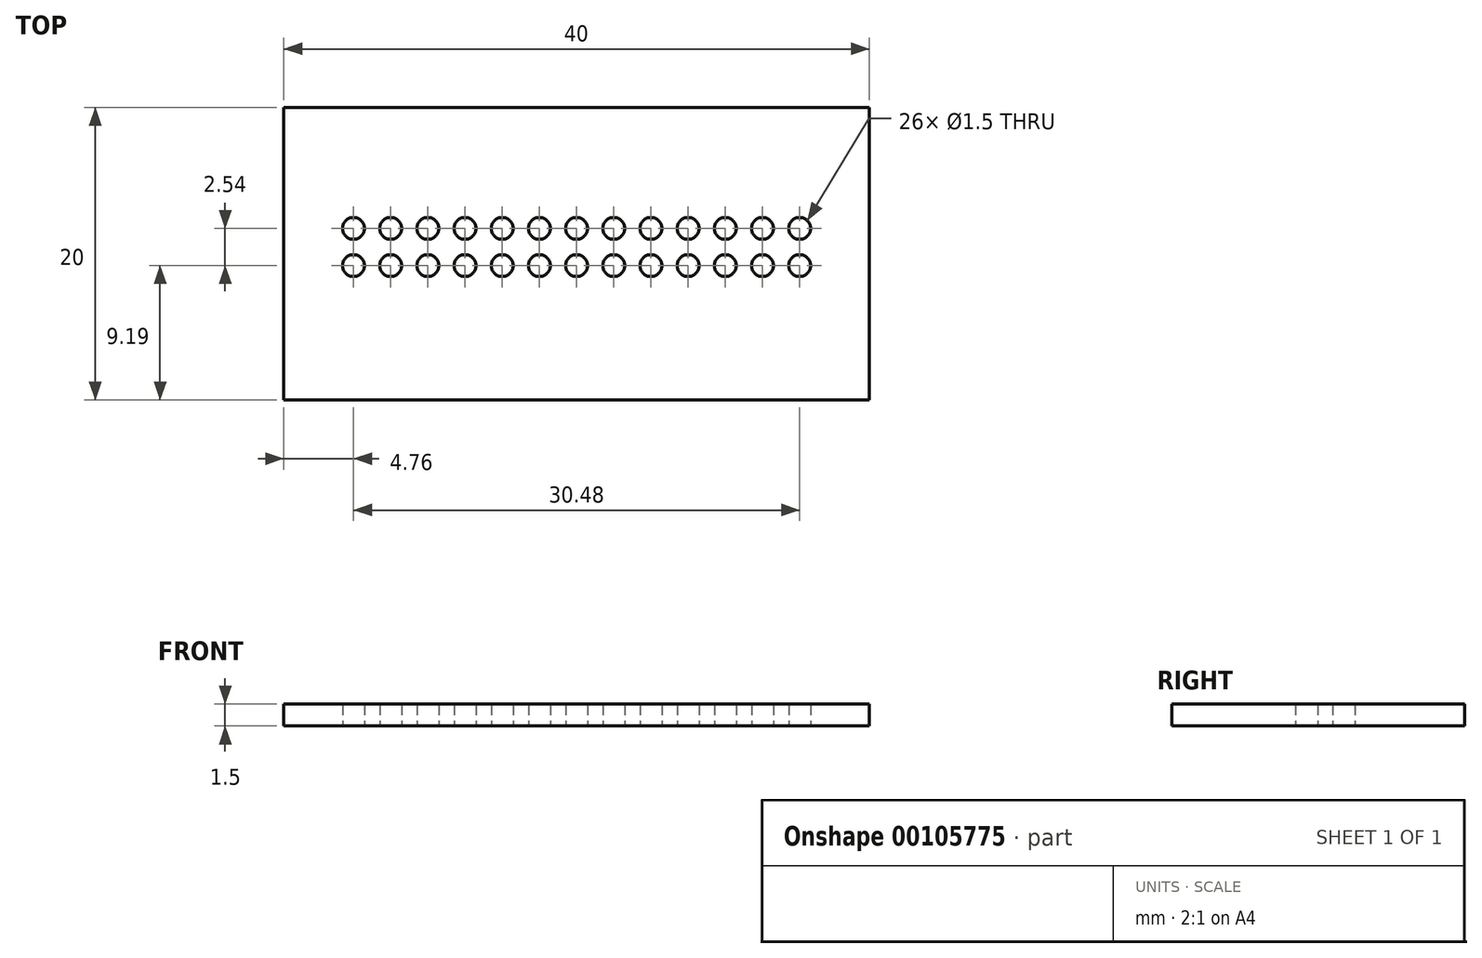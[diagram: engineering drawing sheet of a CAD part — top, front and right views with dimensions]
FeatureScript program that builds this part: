
annotation { "Feature Type Name" : "Feature", "Feature Type Description" : "" }
export const myFeature = defineFeature(function(context is Context, id is Id, definition is map)
    precondition{}
    {
        {
            var Q0;
            Q0=qCreatedBy(makeId("Top.planeOp"),FACE);
            var sketch = newSketch(context, id + "F0", { "sketchPlane" : qUnion([Q0])});
            skLineSegment(sketch, "E0.bottom", {"start": v(-20, 10) * mm, "end": v(20, 10) * mm});
            skLineSegment(sketch, "E0.top", {"start": v(-20, -10) * mm, "end": v(20, -10) * mm});
            skLineSegment(sketch, "E0.left", {"start": v(-20, 10) * mm, "end": v(-20, -10) * mm});
            skLineSegment(sketch, "E0.right", {"start": v(20, 10) * mm, "end": v(20, -10) * mm});
            skLineSegment(sketch, "E1.bottom", {"start": v(-16.5, 2.96) * mm, "end": v(16.5, 2.96) * mm});
            skLineSegment(sketch, "E1.top", {"start": v(-16.5, -2.04) * mm, "end": v(16.5, -2.04) * mm});
            skLineSegment(sketch, "E1.left", {"start": v(-16.5, 2.96) * mm, "end": v(-16.5, -2.04) * mm});
            skLineSegment(sketch, "E1.right", {"start": v(16.5, 2.96) * mm, "end": v(16.5, -2.04) * mm});
            skLineSegment(sketch, "E2", {"start": v(-16.5, 1.73) * mm, "end": v(16.5, 1.73) * mm});
            skLineSegment(sketch, "E3", {"start": v(-16.5, -0.81) * mm, "end": v(16.5, -0.81) * mm});
            skLineSegment(sketch, "E4", {"start": v(-15.24, 2.96) * mm, "end": v(-15.24, -2.04) * mm});
            skLineSegment(sketch, "E5.1.0.0", {"start": v(-12.7, 2.96) * mm, "end": v(-12.7, -2.04) * mm});
            skLineSegment(sketch, "E5.2.0.0", {"start": v(-10.16, 2.96) * mm, "end": v(-10.16, -2.04) * mm});
            skLineSegment(sketch, "E5.3.0.0", {"start": v(-7.62, 2.96) * mm, "end": v(-7.62, -2.04) * mm});
            skLineSegment(sketch, "E5.4.0.0", {"start": v(-5.08, 2.96) * mm, "end": v(-5.08, -2.04) * mm});
            skLineSegment(sketch, "E5.5.0.0", {"start": v(-2.54, 2.96) * mm, "end": v(-2.54, -2.04) * mm});
            skLineSegment(sketch, "E5.6.0.0", {"start": v(0, 2.96) * mm, "end": v(0, -2.04) * mm});
            skLineSegment(sketch, "E5.7.0.0", {"start": v(2.54, 2.96) * mm, "end": v(2.54, -2.04) * mm});
            skLineSegment(sketch, "E5.8.0.0", {"start": v(5.08, 2.96) * mm, "end": v(5.08, -2.04) * mm});
            skLineSegment(sketch, "E5.9.0.0", {"start": v(7.62, 2.96) * mm, "end": v(7.62, -2.04) * mm});
            skLineSegment(sketch, "E5.10.0.0", {"start": v(10.16, 2.96) * mm, "end": v(10.16, -2.04) * mm});
            skLineSegment(sketch, "E5.11.0.0", {"start": v(12.7, 2.96) * mm, "end": v(12.7, -2.04) * mm});
            skLineSegment(sketch, "E5.12.0.0", {"start": v(15.24, 2.96) * mm, "end": v(15.24, -2.04) * mm});
            skLineSegment(sketch, "E5.direction1", {"start": v(-15.24, -2.04) * mm, "end": v(-12.7, -2.04) * mm, "construction": true});
            skPoint(sketch, "E6", {"position": v(-15.24, 1.73) * mm});
            skPoint(sketch, "E7", {"position": v(-15.24, -0.81) * mm});
            skPoint(sketch, "E8", {"position": v(-12.7, -0.81) * mm});
            skPoint(sketch, "E9", {"position": v(-12.7, 1.73) * mm});
            skPoint(sketch, "E10", {"position": v(-10.16, 1.73) * mm});
            skPoint(sketch, "E11", {"position": v(-10.16, -0.81) * mm});
            skPoint(sketch, "E12", {"position": v(-7.62, -0.81) * mm});
            skPoint(sketch, "E13", {"position": v(-7.62, 1.73) * mm});
            skPoint(sketch, "E14", {"position": v(-5.08, 1.73) * mm});
            skPoint(sketch, "E15", {"position": v(-5.08, -0.81) * mm});
            skPoint(sketch, "E16", {"position": v(-2.54, -0.81) * mm});
            skPoint(sketch, "E17", {"position": v(-2.54, 1.73) * mm});
            skPoint(sketch, "E18", {"position": v(0, 1.73) * mm});
            skPoint(sketch, "E19", {"position": v(0, -0.81) * mm});
            skPoint(sketch, "E20", {"position": v(2.54, -0.81) * mm});
            skPoint(sketch, "E21", {"position": v(2.54, 1.73) * mm});
            skPoint(sketch, "E22", {"position": v(5.08, -0.81) * mm});
            skPoint(sketch, "E23", {"position": v(5.08, 1.73) * mm});
            skPoint(sketch, "E24", {"position": v(7.62, 1.73) * mm});
            skPoint(sketch, "E25", {"position": v(7.62, -0.81) * mm});
            skPoint(sketch, "E26", {"position": v(10.16, -0.81) * mm});
            skPoint(sketch, "E27", {"position": v(10.16, 1.73) * mm});
            skPoint(sketch, "E28", {"position": v(12.7, 1.73) * mm});
            skPoint(sketch, "E29", {"position": v(12.7, -0.81) * mm});
            skPoint(sketch, "E30", {"position": v(15.24, 1.73) * mm});
            skPoint(sketch, "E31", {"position": v(15.24, -0.81) * mm});
            skSolve(sketch);
        }
        {
            var Q0;
            Q0=makeQuery(id+"F0.imprint","IMPRINT",FACE,{"disambiguationData":[TD([[makeQuery(id+"F0.imprint","IMPRINT",EDGE,{"derivedFrom":sQuery(id+"F0.wireOp",EDGE,"E0.bottom")}),-1.0]])]});
            var Q1;
            {var subQ0=sQuery(id+"F0.wireOp",EDGE,"E5.1.0.0");var subQ1=sQuery(id+"F0.wireOp",EDGE,"E1.bottom");var subQ2=makeQuery(id+"F0.imprint","INTERSECT",VERTEX,{"derivedFrom":[subQ1,subQ0]});Q1=makeQuery(id+"F0.imprint","IMPRINT",FACE,{"disambiguationData":[TD([[makeQuery(id+"F0.imprint","IMPRINT",EDGE,{"disambiguationData":[TD([[subQ2,-1.0]])],"derivedFrom":subQ1}),-1.0]])]});}
            var Q2;
            {var subQ0=sQuery(id+"F0.wireOp",EDGE,"E4");var subQ1=sQuery(id+"F0.wireOp",EDGE,"E1.bottom");var subQ2=makeQuery(id+"F0.imprint","INTERSECT",VERTEX,{"derivedFrom":[subQ1,subQ0]});Q2=makeQuery(id+"F0.imprint","IMPRINT",FACE,{"disambiguationData":[TD([[makeQuery(id+"F0.imprint","IMPRINT",EDGE,{"disambiguationData":[TD([[subQ2,-1.0]])],"derivedFrom":subQ1}),-1.0]])]});}
            var Q3;
            {var subQ0=sQuery(id+"F0.wireOp",EDGE,"E5.6.0.0");var subQ1=sQuery(id+"F0.wireOp",EDGE,"E2");var subQ2=makeQuery(id+"F0.imprint","INTERSECT",VERTEX,{"derivedFrom":[subQ1,subQ0]});Q3=makeQuery(id+"F0.imprint","IMPRINT",FACE,{"disambiguationData":[TD([[makeQuery(id+"F0.imprint","IMPRINT",EDGE,{"disambiguationData":[TD([[subQ2,-1.0]])],"derivedFrom":subQ1}),-1.0]])]});}
            var Q4;
            {var subQ0=sQuery(id+"F0.wireOp",EDGE,"E5.5.0.0");var subQ1=sQuery(id+"F0.wireOp",EDGE,"E1.top");var subQ2=makeQuery(id+"F0.imprint","INTERSECT",VERTEX,{"derivedFrom":[subQ1,subQ0]});Q4=makeQuery(id+"F0.imprint","IMPRINT",FACE,{"disambiguationData":[TD([[makeQuery(id+"F0.imprint","IMPRINT",EDGE,{"disambiguationData":[TD([[subQ2,-1.0]])],"derivedFrom":subQ1}),1.0]])]});}
            var Q5;
            {var subQ0=sQuery(id+"F0.wireOp",EDGE,"E5.11.0.0");var subQ1=sQuery(id+"F0.wireOp",EDGE,"E1.top");var subQ2=makeQuery(id+"F0.imprint","INTERSECT",VERTEX,{"derivedFrom":[subQ1,subQ0]});Q5=makeQuery(id+"F0.imprint","IMPRINT",FACE,{"disambiguationData":[TD([[makeQuery(id+"F0.imprint","IMPRINT",EDGE,{"disambiguationData":[TD([[subQ2,-1.0]])],"derivedFrom":subQ1}),1.0]])]});}
            var Q6;
            {var subQ0=sQuery(id+"F0.wireOp",EDGE,"E5.11.0.0");var subQ1=sQuery(id+"F0.wireOp",EDGE,"E1.bottom");var subQ2=makeQuery(id+"F0.imprint","INTERSECT",VERTEX,{"derivedFrom":[subQ1,subQ0]});Q6=makeQuery(id+"F0.imprint","IMPRINT",FACE,{"disambiguationData":[TD([[makeQuery(id+"F0.imprint","IMPRINT",EDGE,{"disambiguationData":[TD([[subQ2,-1.0]])],"derivedFrom":subQ1}),-1.0]])]});}
            var Q7;
            {var subQ0=sQuery(id+"F0.wireOp",EDGE,"E2");var subQ1=sQuery(id+"F0.wireOp",EDGE,"E1.left");var subQ2=makeQuery(id+"F0.imprint","INTERSECT",VERTEX,{"derivedFrom":[subQ1,subQ0]});Q7=makeQuery(id+"F0.imprint","IMPRINT",FACE,{"disambiguationData":[TD([[makeQuery(id+"F0.imprint","IMPRINT",EDGE,{"disambiguationData":[TD([[subQ2,-1.0]])],"derivedFrom":subQ1}),1.0]])]});}
            var Q8;
            {var subQ0=sQuery(id+"F0.wireOp",EDGE,"E5.8.0.0");var subQ1=sQuery(id+"F0.wireOp",EDGE,"E2");var subQ2=makeQuery(id+"F0.imprint","INTERSECT",VERTEX,{"derivedFrom":[subQ1,subQ0]});Q8=makeQuery(id+"F0.imprint","IMPRINT",FACE,{"disambiguationData":[TD([[makeQuery(id+"F0.imprint","IMPRINT",EDGE,{"disambiguationData":[TD([[subQ2,-1.0]])],"derivedFrom":subQ1}),-1.0]])]});}
            var Q9;
            {var subQ0=sQuery(id+"F0.wireOp",EDGE,"E5.8.0.0");var subQ1=sQuery(id+"F0.wireOp",EDGE,"E1.top");var subQ2=makeQuery(id+"F0.imprint","INTERSECT",VERTEX,{"derivedFrom":[subQ1,subQ0]});Q9=makeQuery(id+"F0.imprint","IMPRINT",FACE,{"disambiguationData":[TD([[makeQuery(id+"F0.imprint","IMPRINT",EDGE,{"disambiguationData":[TD([[subQ2,-1.0]])],"derivedFrom":subQ1}),1.0]])]});}
            var Q10;
            {var subQ0=sQuery(id+"F0.wireOp",EDGE,"E5.7.0.0");var subQ1=sQuery(id+"F0.wireOp",EDGE,"E1.top");var subQ2=makeQuery(id+"F0.imprint","INTERSECT",VERTEX,{"derivedFrom":[subQ1,subQ0]});Q10=makeQuery(id+"F0.imprint","IMPRINT",FACE,{"disambiguationData":[TD([[makeQuery(id+"F0.imprint","IMPRINT",EDGE,{"disambiguationData":[TD([[subQ2,-1.0]])],"derivedFrom":subQ1}),1.0]])]});}
            var Q11;
            {var subQ0=sQuery(id+"F0.wireOp",EDGE,"E5.9.0.0");var subQ1=sQuery(id+"F0.wireOp",EDGE,"E2");var subQ2=makeQuery(id+"F0.imprint","INTERSECT",VERTEX,{"derivedFrom":[subQ1,subQ0]});Q11=makeQuery(id+"F0.imprint","IMPRINT",FACE,{"disambiguationData":[TD([[makeQuery(id+"F0.imprint","IMPRINT",EDGE,{"disambiguationData":[TD([[subQ2,-1.0]])],"derivedFrom":subQ1}),-1.0]])]});}
            var Q12;
            {var subQ0=sQuery(id+"F0.wireOp",EDGE,"E5.6.0.0");var subQ1=sQuery(id+"F0.wireOp",EDGE,"E1.top");var subQ2=makeQuery(id+"F0.imprint","INTERSECT",VERTEX,{"derivedFrom":[subQ1,subQ0]});Q12=makeQuery(id+"F0.imprint","IMPRINT",FACE,{"disambiguationData":[TD([[makeQuery(id+"F0.imprint","IMPRINT",EDGE,{"disambiguationData":[TD([[subQ2,-1.0]])],"derivedFrom":subQ1}),1.0]])]});}
            var Q13;
            {var subQ0=sQuery(id+"F0.wireOp",EDGE,"E5.2.0.0");var subQ1=sQuery(id+"F0.wireOp",EDGE,"E2");var subQ2=makeQuery(id+"F0.imprint","INTERSECT",VERTEX,{"derivedFrom":[subQ1,subQ0]});Q13=makeQuery(id+"F0.imprint","IMPRINT",FACE,{"disambiguationData":[TD([[makeQuery(id+"F0.imprint","IMPRINT",EDGE,{"disambiguationData":[TD([[subQ2,-1.0]])],"derivedFrom":subQ1}),-1.0]])]});}
            var Q14;
            {var subQ0=sQuery(id+"F0.wireOp",EDGE,"E5.4.0.0");var subQ1=sQuery(id+"F0.wireOp",EDGE,"E1.top");var subQ2=makeQuery(id+"F0.imprint","INTERSECT",VERTEX,{"derivedFrom":[subQ1,subQ0]});Q14=makeQuery(id+"F0.imprint","IMPRINT",FACE,{"disambiguationData":[TD([[makeQuery(id+"F0.imprint","IMPRINT",EDGE,{"disambiguationData":[TD([[subQ2,-1.0]])],"derivedFrom":subQ1}),1.0]])]});}
            var Q15;
            {var subQ0=sQuery(id+"F0.wireOp",EDGE,"E5.10.0.0");var subQ1=sQuery(id+"F0.wireOp",EDGE,"E1.bottom");var subQ2=makeQuery(id+"F0.imprint","INTERSECT",VERTEX,{"derivedFrom":[subQ1,subQ0]});Q15=makeQuery(id+"F0.imprint","IMPRINT",FACE,{"disambiguationData":[TD([[makeQuery(id+"F0.imprint","IMPRINT",EDGE,{"disambiguationData":[TD([[subQ2,-1.0]])],"derivedFrom":subQ1}),-1.0]])]});}
            var Q16;
            {var subQ0=sQuery(id+"F0.wireOp",EDGE,"E4");var subQ1=sQuery(id+"F0.wireOp",EDGE,"E1.top");var subQ2=makeQuery(id+"F0.imprint","INTERSECT",VERTEX,{"derivedFrom":[subQ1,subQ0]});Q16=makeQuery(id+"F0.imprint","IMPRINT",FACE,{"disambiguationData":[TD([[makeQuery(id+"F0.imprint","IMPRINT",EDGE,{"disambiguationData":[TD([[subQ2,-1.0]])],"derivedFrom":subQ1}),1.0]])]});}
            var Q17;
            {var subQ0=sQuery(id+"F0.wireOp",EDGE,"E5.9.0.0");var subQ1=sQuery(id+"F0.wireOp",EDGE,"E1.bottom");var subQ2=makeQuery(id+"F0.imprint","INTERSECT",VERTEX,{"derivedFrom":[subQ1,subQ0]});Q17=makeQuery(id+"F0.imprint","IMPRINT",FACE,{"disambiguationData":[TD([[makeQuery(id+"F0.imprint","IMPRINT",EDGE,{"disambiguationData":[TD([[subQ2,-1.0]])],"derivedFrom":subQ1}),-1.0]])]});}
            var Q18;
            {var subQ0=sQuery(id+"F0.wireOp",EDGE,"E5.4.0.0");var subQ1=sQuery(id+"F0.wireOp",EDGE,"E1.bottom");var subQ2=makeQuery(id+"F0.imprint","INTERSECT",VERTEX,{"derivedFrom":[subQ1,subQ0]});Q18=makeQuery(id+"F0.imprint","IMPRINT",FACE,{"disambiguationData":[TD([[makeQuery(id+"F0.imprint","IMPRINT",EDGE,{"disambiguationData":[TD([[subQ2,-1.0]])],"derivedFrom":subQ1}),-1.0]])]});}
            var Q19;
            {var subQ0=sQuery(id+"F0.wireOp",EDGE,"E5.3.0.0");var subQ1=sQuery(id+"F0.wireOp",EDGE,"E1.bottom");var subQ2=makeQuery(id+"F0.imprint","INTERSECT",VERTEX,{"derivedFrom":[subQ1,subQ0]});Q19=makeQuery(id+"F0.imprint","IMPRINT",FACE,{"disambiguationData":[TD([[makeQuery(id+"F0.imprint","IMPRINT",EDGE,{"disambiguationData":[TD([[subQ2,-1.0]])],"derivedFrom":subQ1}),-1.0]])]});}
            var Q20;
            {var subQ0=sQuery(id+"F0.wireOp",EDGE,"E5.6.0.0");var subQ1=sQuery(id+"F0.wireOp",EDGE,"E1.bottom");var subQ2=makeQuery(id+"F0.imprint","INTERSECT",VERTEX,{"derivedFrom":[subQ1,subQ0]});Q20=makeQuery(id+"F0.imprint","IMPRINT",FACE,{"disambiguationData":[TD([[makeQuery(id+"F0.imprint","IMPRINT",EDGE,{"disambiguationData":[TD([[subQ2,-1.0]])],"derivedFrom":subQ1}),-1.0]])]});}
            var Q21;
            {var subQ0=sQuery(id+"F0.wireOp",EDGE,"E5.7.0.0");var subQ1=sQuery(id+"F0.wireOp",EDGE,"E1.bottom");var subQ2=makeQuery(id+"F0.imprint","INTERSECT",VERTEX,{"derivedFrom":[subQ1,subQ0]});Q21=makeQuery(id+"F0.imprint","IMPRINT",FACE,{"disambiguationData":[TD([[makeQuery(id+"F0.imprint","IMPRINT",EDGE,{"disambiguationData":[TD([[subQ2,-1.0]])],"derivedFrom":subQ1}),-1.0]])]});}
            var Q22;
            {var subQ0=sQuery(id+"F0.wireOp",EDGE,"E2");var subQ1=sQuery(id+"F0.wireOp",EDGE,"E1.right");var subQ2=makeQuery(id+"F0.imprint","INTERSECT",VERTEX,{"derivedFrom":[subQ1,subQ0]});Q22=makeQuery(id+"F0.imprint","IMPRINT",FACE,{"disambiguationData":[TD([[makeQuery(id+"F0.imprint","IMPRINT",EDGE,{"disambiguationData":[TD([[subQ2,-1.0]])],"derivedFrom":subQ1}),-1.0]])]});}
            var Q23;
            {var subQ0=sQuery(id+"F0.wireOp",EDGE,"E5.5.0.0");var subQ1=sQuery(id+"F0.wireOp",EDGE,"E1.bottom");var subQ2=makeQuery(id+"F0.imprint","INTERSECT",VERTEX,{"derivedFrom":[subQ1,subQ0]});Q23=makeQuery(id+"F0.imprint","IMPRINT",FACE,{"disambiguationData":[TD([[makeQuery(id+"F0.imprint","IMPRINT",EDGE,{"disambiguationData":[TD([[subQ2,-1.0]])],"derivedFrom":subQ1}),-1.0]])]});}
            var Q24;
            {var subQ0=sQuery(id+"F0.wireOp",EDGE,"E5.2.0.0");var subQ1=sQuery(id+"F0.wireOp",EDGE,"E1.bottom");var subQ2=makeQuery(id+"F0.imprint","INTERSECT",VERTEX,{"derivedFrom":[subQ1,subQ0]});Q24=makeQuery(id+"F0.imprint","IMPRINT",FACE,{"disambiguationData":[TD([[makeQuery(id+"F0.imprint","IMPRINT",EDGE,{"disambiguationData":[TD([[subQ2,-1.0]])],"derivedFrom":subQ1}),-1.0]])]});}
            var Q25;
            {var subQ0=sQuery(id+"F0.wireOp",EDGE,"E5.8.0.0");var subQ1=sQuery(id+"F0.wireOp",EDGE,"E1.bottom");var subQ2=makeQuery(id+"F0.imprint","INTERSECT",VERTEX,{"derivedFrom":[subQ1,subQ0]});Q25=makeQuery(id+"F0.imprint","IMPRINT",FACE,{"disambiguationData":[TD([[makeQuery(id+"F0.imprint","IMPRINT",EDGE,{"disambiguationData":[TD([[subQ2,-1.0]])],"derivedFrom":subQ1}),-1.0]])]});}
            var Q26;
            {var subQ0=sQuery(id+"F0.wireOp",EDGE,"E5.4.0.0");var subQ1=sQuery(id+"F0.wireOp",EDGE,"E2");var subQ2=makeQuery(id+"F0.imprint","INTERSECT",VERTEX,{"derivedFrom":[subQ1,subQ0]});Q26=makeQuery(id+"F0.imprint","IMPRINT",FACE,{"disambiguationData":[TD([[makeQuery(id+"F0.imprint","IMPRINT",EDGE,{"disambiguationData":[TD([[subQ2,-1.0]])],"derivedFrom":subQ1}),-1.0]])]});}
            var Q27;
            {var subQ0=sQuery(id+"F0.wireOp",EDGE,"E5.2.0.0");var subQ1=sQuery(id+"F0.wireOp",EDGE,"E1.top");var subQ2=makeQuery(id+"F0.imprint","INTERSECT",VERTEX,{"derivedFrom":[subQ1,subQ0]});Q27=makeQuery(id+"F0.imprint","IMPRINT",FACE,{"disambiguationData":[TD([[makeQuery(id+"F0.imprint","IMPRINT",EDGE,{"disambiguationData":[TD([[subQ2,-1.0]])],"derivedFrom":subQ1}),1.0]])]});}
            var Q28;
            {var subQ0=sQuery(id+"F0.wireOp",EDGE,"E4");var subQ1=sQuery(id+"F0.wireOp",EDGE,"E2");var subQ2=makeQuery(id+"F0.imprint","INTERSECT",VERTEX,{"derivedFrom":[subQ1,subQ0]});Q28=makeQuery(id+"F0.imprint","IMPRINT",FACE,{"disambiguationData":[TD([[makeQuery(id+"F0.imprint","IMPRINT",EDGE,{"disambiguationData":[TD([[subQ2,-1.0]])],"derivedFrom":subQ1}),-1.0]])]});}
            var Q29;
            {var subQ0=sQuery(id+"F0.wireOp",EDGE,"E5.7.0.0");var subQ1=sQuery(id+"F0.wireOp",EDGE,"E2");var subQ2=makeQuery(id+"F0.imprint","INTERSECT",VERTEX,{"derivedFrom":[subQ1,subQ0]});Q29=makeQuery(id+"F0.imprint","IMPRINT",FACE,{"disambiguationData":[TD([[makeQuery(id+"F0.imprint","IMPRINT",EDGE,{"disambiguationData":[TD([[subQ2,-1.0]])],"derivedFrom":subQ1}),-1.0]])]});}
            var Q30;
            {var subQ0=sQuery(id+"F0.wireOp",EDGE,"E5.1.0.0");var subQ1=sQuery(id+"F0.wireOp",EDGE,"E2");var subQ2=makeQuery(id+"F0.imprint","INTERSECT",VERTEX,{"derivedFrom":[subQ1,subQ0]});Q30=makeQuery(id+"F0.imprint","IMPRINT",FACE,{"disambiguationData":[TD([[makeQuery(id+"F0.imprint","IMPRINT",EDGE,{"disambiguationData":[TD([[subQ2,-1.0]])],"derivedFrom":subQ1}),-1.0]])]});}
            var Q31;
            {var subQ0=sQuery(id+"F0.wireOp",EDGE,"E5.1.0.0");var subQ1=sQuery(id+"F0.wireOp",EDGE,"E1.top");var subQ2=makeQuery(id+"F0.imprint","INTERSECT",VERTEX,{"derivedFrom":[subQ1,subQ0]});Q31=makeQuery(id+"F0.imprint","IMPRINT",FACE,{"disambiguationData":[TD([[makeQuery(id+"F0.imprint","IMPRINT",EDGE,{"disambiguationData":[TD([[subQ2,-1.0]])],"derivedFrom":subQ1}),1.0]])]});}
            var Q32;
            {var subQ0=sQuery(id+"F0.wireOp",EDGE,"E5.10.0.0");var subQ1=sQuery(id+"F0.wireOp",EDGE,"E1.top");var subQ2=makeQuery(id+"F0.imprint","INTERSECT",VERTEX,{"derivedFrom":[subQ1,subQ0]});Q32=makeQuery(id+"F0.imprint","IMPRINT",FACE,{"disambiguationData":[TD([[makeQuery(id+"F0.imprint","IMPRINT",EDGE,{"disambiguationData":[TD([[subQ2,-1.0]])],"derivedFrom":subQ1}),1.0]])]});}
            var Q33;
            {var subQ0=sQuery(id+"F0.wireOp",EDGE,"E5.3.0.0");var subQ1=sQuery(id+"F0.wireOp",EDGE,"E2");var subQ2=makeQuery(id+"F0.imprint","INTERSECT",VERTEX,{"derivedFrom":[subQ1,subQ0]});Q33=makeQuery(id+"F0.imprint","IMPRINT",FACE,{"disambiguationData":[TD([[makeQuery(id+"F0.imprint","IMPRINT",EDGE,{"disambiguationData":[TD([[subQ2,-1.0]])],"derivedFrom":subQ1}),-1.0]])]});}
            var Q34;
            {var subQ0=sQuery(id+"F0.wireOp",EDGE,"E5.5.0.0");var subQ1=sQuery(id+"F0.wireOp",EDGE,"E2");var subQ2=makeQuery(id+"F0.imprint","INTERSECT",VERTEX,{"derivedFrom":[subQ1,subQ0]});Q34=makeQuery(id+"F0.imprint","IMPRINT",FACE,{"disambiguationData":[TD([[makeQuery(id+"F0.imprint","IMPRINT",EDGE,{"disambiguationData":[TD([[subQ2,-1.0]])],"derivedFrom":subQ1}),-1.0]])]});}
            var Q35;
            {var subQ0=sQuery(id+"F0.wireOp",EDGE,"E5.11.0.0");var subQ1=sQuery(id+"F0.wireOp",EDGE,"E2");var subQ2=makeQuery(id+"F0.imprint","INTERSECT",VERTEX,{"derivedFrom":[subQ1,subQ0]});Q35=makeQuery(id+"F0.imprint","IMPRINT",FACE,{"disambiguationData":[TD([[makeQuery(id+"F0.imprint","IMPRINT",EDGE,{"disambiguationData":[TD([[subQ2,-1.0]])],"derivedFrom":subQ1}),-1.0]])]});}
            var Q36;
            {var subQ0=sQuery(id+"F0.wireOp",EDGE,"E5.10.0.0");var subQ1=sQuery(id+"F0.wireOp",EDGE,"E2");var subQ2=makeQuery(id+"F0.imprint","INTERSECT",VERTEX,{"derivedFrom":[subQ1,subQ0]});Q36=makeQuery(id+"F0.imprint","IMPRINT",FACE,{"disambiguationData":[TD([[makeQuery(id+"F0.imprint","IMPRINT",EDGE,{"disambiguationData":[TD([[subQ2,-1.0]])],"derivedFrom":subQ1}),-1.0]])]});}
            var Q37;
            {var subQ0=sQuery(id+"F0.wireOp",EDGE,"E5.9.0.0");var subQ1=sQuery(id+"F0.wireOp",EDGE,"E1.top");var subQ2=makeQuery(id+"F0.imprint","INTERSECT",VERTEX,{"derivedFrom":[subQ1,subQ0]});Q37=makeQuery(id+"F0.imprint","IMPRINT",FACE,{"disambiguationData":[TD([[makeQuery(id+"F0.imprint","IMPRINT",EDGE,{"disambiguationData":[TD([[subQ2,-1.0]])],"derivedFrom":subQ1}),1.0]])]});}
            var Q38;
            {var subQ0=sQuery(id+"F0.wireOp",EDGE,"E5.3.0.0");var subQ1=sQuery(id+"F0.wireOp",EDGE,"E1.top");var subQ2=makeQuery(id+"F0.imprint","INTERSECT",VERTEX,{"derivedFrom":[subQ1,subQ0]});Q38=makeQuery(id+"F0.imprint","IMPRINT",FACE,{"disambiguationData":[TD([[makeQuery(id+"F0.imprint","IMPRINT",EDGE,{"disambiguationData":[TD([[subQ2,-1.0]])],"derivedFrom":subQ1}),1.0]])]});}
            var Q39;
            {var subQ0=sQuery(id+"F0.wireOp",EDGE,"E1.right");var subQ1=sQuery(id+"F0.wireOp",EDGE,"E1.top");var subQ2=makeQuery(id+"F0.imprint","INTERSECT",VERTEX,{"derivedFrom":[subQ1,subQ0]});Q39=makeQuery(id+"F0.imprint","IMPRINT",FACE,{"disambiguationData":[TD([[makeQuery(id+"F0.imprint","IMPRINT",EDGE,{"disambiguationData":[TD([[subQ2,1.0]])],"derivedFrom":subQ1}),1.0]])]});}
            var Q40;
            {var subQ0=sQuery(id+"F0.wireOp",EDGE,"E1.left");var subQ1=sQuery(id+"F0.wireOp",EDGE,"E1.top");var subQ2=makeQuery(id+"F0.imprint","INTERSECT",VERTEX,{"derivedFrom":[subQ1,subQ0]});Q40=makeQuery(id+"F0.imprint","IMPRINT",FACE,{"disambiguationData":[TD([[makeQuery(id+"F0.imprint","IMPRINT",EDGE,{"disambiguationData":[TD([[subQ2,-1.0]])],"derivedFrom":subQ1}),1.0]])]});}
            var Q41;
            {var subQ0=sQuery(id+"F0.wireOp",EDGE,"E1.right");var subQ1=sQuery(id+"F0.wireOp",EDGE,"E1.bottom");var subQ2=makeQuery(id+"F0.imprint","INTERSECT",VERTEX,{"derivedFrom":[subQ1,subQ0]});Q41=makeQuery(id+"F0.imprint","IMPRINT",FACE,{"disambiguationData":[TD([[makeQuery(id+"F0.imprint","IMPRINT",EDGE,{"disambiguationData":[TD([[subQ2,1.0]])],"derivedFrom":subQ1}),-1.0]])]});}
            var Q42;
            {var subQ0=sQuery(id+"F0.wireOp",EDGE,"E1.left");var subQ1=sQuery(id+"F0.wireOp",EDGE,"E1.bottom");var subQ2=makeQuery(id+"F0.imprint","INTERSECT",VERTEX,{"derivedFrom":[subQ1,subQ0]});Q42=makeQuery(id+"F0.imprint","IMPRINT",FACE,{"disambiguationData":[TD([[makeQuery(id+"F0.imprint","IMPRINT",EDGE,{"disambiguationData":[TD([[subQ2,-1.0]])],"derivedFrom":subQ1}),-1.0]])]});}
            extrude(context, id + "F1", {"entities" : qUnion([Q0, Q1, Q2, Q3, Q4, Q5, Q6, Q7, Q8, Q9, Q10, Q11, Q12, Q13, Q14, Q15, Q16, Q17, Q18, Q19, Q20, Q21, Q22, Q23, Q24, Q25, Q26, Q27, Q28, Q29, Q30, Q31, Q32, Q33, Q34, Q35, Q36, Q37, Q38, Q39, Q40, Q41, Q42]), "depth" : 1.5 * mm});
        }
        {
            var Q0;
            Q0=sQuery(id+"F0.wireOp",VERTEX,"E28");
            var Q1;
            Q1=sQuery(id+"F0.wireOp",VERTEX,"E29");
            var Q2;
            Q2=sQuery(id+"F0.wireOp",VERTEX,"E31");
            var Q3;
            Q3=sQuery(id+"F0.wireOp",VERTEX,"E30");
            var Q4;
            Q4=sQuery(id+"F0.wireOp",VERTEX,"E27");
            var Q5;
            Q5=sQuery(id+"F0.wireOp",VERTEX,"E26");
            var Q6;
            Q6=sQuery(id+"F0.wireOp",VERTEX,"E25");
            var Q7;
            Q7=sQuery(id+"F0.wireOp",VERTEX,"E24");
            var Q8;
            Q8=sQuery(id+"F0.wireOp",VERTEX,"E23");
            var Q9;
            Q9=sQuery(id+"F0.wireOp",VERTEX,"E22");
            var Q10;
            Q10=sQuery(id+"F0.wireOp",VERTEX,"E20");
            var Q11;
            Q11=sQuery(id+"F0.wireOp",VERTEX,"E21");
            var Q12;
            Q12=sQuery(id+"F0.wireOp",VERTEX,"E18");
            var Q13;
            Q13=sQuery(id+"F0.wireOp",VERTEX,"E19");
            var Q14;
            Q14=sQuery(id+"F0.wireOp",VERTEX,"E16");
            var Q15;
            Q15=sQuery(id+"F0.wireOp",VERTEX,"E17");
            var Q16;
            Q16=sQuery(id+"F0.wireOp",VERTEX,"E14");
            var Q17;
            Q17=sQuery(id+"F0.wireOp",VERTEX,"E15");
            var Q18;
            Q18=sQuery(id+"F0.wireOp",VERTEX,"E12");
            var Q19;
            Q19=sQuery(id+"F0.wireOp",VERTEX,"E13");
            var Q20;
            Q20=sQuery(id+"F0.wireOp",VERTEX,"E10");
            var Q21;
            Q21=sQuery(id+"F0.wireOp",VERTEX,"E11");
            var Q22;
            Q22=sQuery(id+"F0.wireOp",VERTEX,"E8");
            var Q23;
            Q23=sQuery(id+"F0.wireOp",VERTEX,"E9");
            var Q24;
            Q24=sQuery(id+"F0.wireOp",VERTEX,"E6");
            var Q25;
            Q25=sQuery(id+"F0.wireOp",VERTEX,"E7");
            var Q26;
            Q26=makeQuery(id+"F1.opExtrude","SWEPT_BODY",BODY,{"disambiguationData":[OSD([sQuery(id+"F0.wireOp",EDGE,"E0.bottom"),sQuery(id+"F0.wireOp",EDGE,"E0.top"),sQuery(id+"F0.wireOp",EDGE,"E0.left"),sQuery(id+"F0.wireOp",EDGE,"E0.right")])]});
            hole(context, id + "F2", {"style" : HoleStyle.SIMPLE, "endStyle" : HoleEndStyle.THROUGH, "oppositeDirection" : true, "holeDiameter" : 1.5 * mm, "locations" : qUnion([Q0, Q1, Q2, Q3, Q4, Q5, Q6, Q7, Q8, Q9, Q10, Q11, Q12, Q13, Q14, Q15, Q16, Q17, Q18, Q19, Q20, Q21, Q22, Q23, Q24, Q25]), "scope" : qUnion([Q26]), "isTappedThrough" : true});
        }
    });
